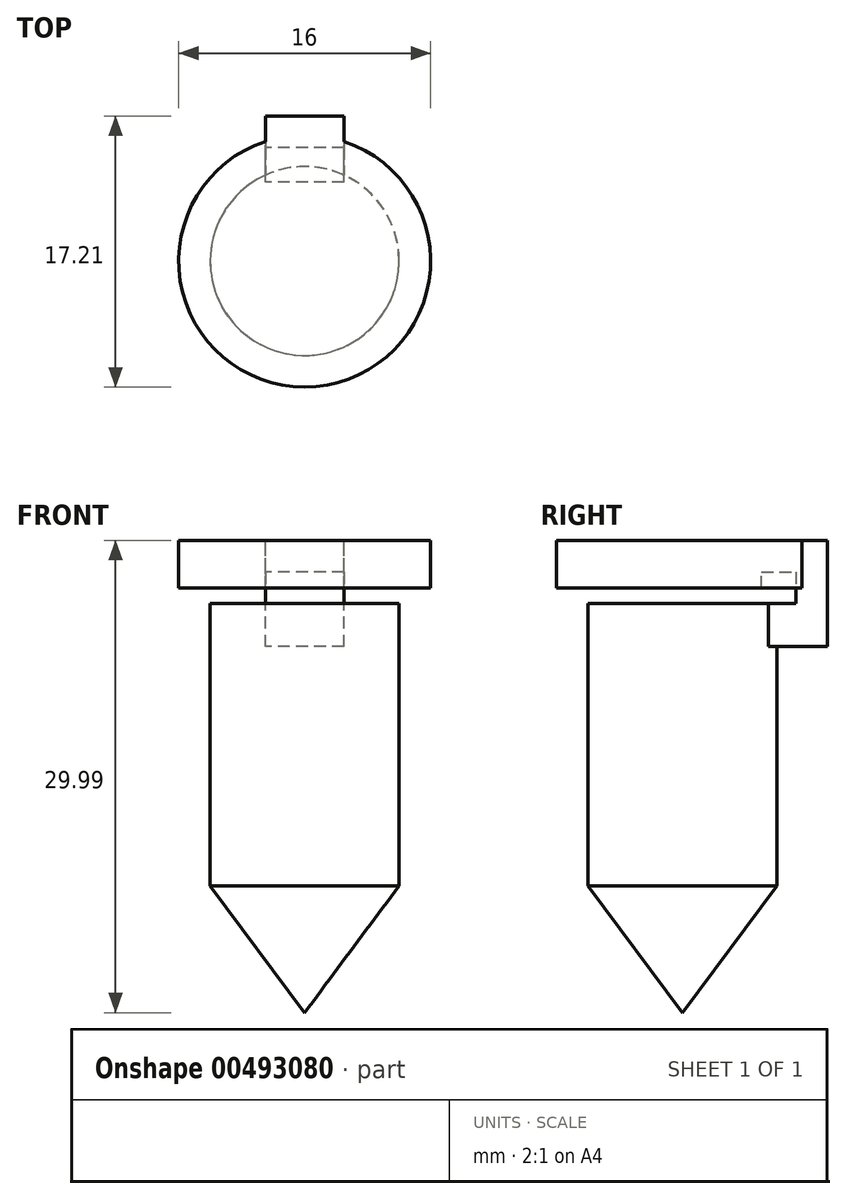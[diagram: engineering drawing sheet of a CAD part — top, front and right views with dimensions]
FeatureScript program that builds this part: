
annotation { "Feature Type Name" : "Feature", "Feature Type Description" : "" }
export const myFeature = defineFeature(function(context is Context, id is Id, definition is map)
    precondition{}
    {
        {
            var Q0;
            Q0=qCreatedBy(makeId("Front.planeOp"),FACE);
            var sketch = newSketch(context, id + "F0", { "sketchPlane" : qUnion([Q0])});
            skLineSegment(sketch, "E0", {"start": v(-6, 14.04) * mm, "end": v(-6, -3.88) * mm});
            skLineSegment(sketch, "E1", {"start": v(-6, -3.88) * mm, "end": v(0, -11.95) * mm});
            skLineSegment(sketch, "E2", {"start": v(-6, 14.04) * mm, "end": v(0, 14.04) * mm});
            skLineSegment(sketch, "E3", {"start": v(0, 14.04) * mm, "end": v(0, -11.95) * mm});
            skSolve(sketch);
        }
        {
            var Q0;
            Q0=makeQuery(id+"F0.imprint","IMPRINT",FACE,{"disambiguationData":[TD([[makeQuery(id+"F0.imprint","IMPRINT",EDGE,{"derivedFrom":sQuery(id+"F0.wireOp",EDGE,"E0")}),1.0]])]});
            var Q1;
            Q1=sQuery(id+"F0.wireOp",EDGE,"E3");
            revolve(context, id + "F1", {"entities" : qUnion([Q0]), "axis" : qUnion([Q1]), "revolveType" : RevolveType.FULL});
        }
        {
            var Q0;
            Q0=qCreatedBy(makeId("Right.planeOp"),FACE);
            var sketch = newSketch(context, id + "F2", { "sketchPlane" : qUnion([Q0])});
            skLineSegment(sketch, "E4", {"start": v(5.2, 11.3) * mm, "end": v(9.2, 11.3) * mm});
            skLineSegment(sketch, "E5", {"start": v(9.2, 11.3) * mm, "end": v(9.2, 18.04) * mm});
            skLineSegment(sketch, "E6", {"start": v(9.2, 18.04) * mm, "end": v(5.01, 18.04) * mm});
            skLineSegment(sketch, "E7", {"start": v(5.01, 18.04) * mm, "end": v(5.01, 16.04) * mm});
            skLineSegment(sketch, "E8", {"start": v(5.01, 16.04) * mm, "end": v(7.2, 16.04) * mm});
            skLineSegment(sketch, "E9", {"start": v(7.2, 16.04) * mm, "end": v(7.2, 14.04) * mm});
            skLineSegment(sketch, "E10", {"start": v(7.2, 14.04) * mm, "end": v(5.01, 14.04) * mm});
            skLineSegment(sketch, "E11", {"start": v(5.01, 14.04) * mm, "end": v(5.2, 11.3) * mm});
            skSolve(sketch);
        }
        {
            var Q0;
            Q0=makeQuery(id+"F2.imprint","IMPRINT",FACE,{"disambiguationData":[TD([[makeQuery(id+"F2.imprint","IMPRINT",EDGE,{"derivedFrom":sQuery(id+"F2.wireOp",EDGE,"E4")}),1.0]])]});
            extrude(context, id + "F3", {"entities" : qUnion([Q0]), "operationType" : NewBodyOperationType.ADD, "endBound" : BoundingType.SYMMETRIC, "depth" : 5 * mm});
        }
        {
            var Q0;
            Q0=makeQuery(id+"F3.opExtrude","SWEPT_FACE",FACE,{"disambiguationData":[OSD([sQuery(id+"F2.wireOp",EDGE,"E6")])]});
            var sketch = newSketch(context, id + "F4", { "sketchPlane" : qUnion([Q0])});
            skCircle(sketch, "E12", {"center": v(0, 0) * mm, "radius": 8 * mm});
            skSolve(sketch);
        }
        {
            var Q0;
            {var subQ1=sQuery(id+"F2.wireOp",EDGE,"E6");var subQ6=makeQuery(id+"F3.opExtrude","SWEPT_EDGE",EDGE,{"disambiguationData":[OSD([subQ1,sQuery(id+"F2.wireOp",EDGE,"E7")])]});Q0=makeQuery(id+"F4.imprint","IMPRINT",FACE,{"disambiguationData":[TD([[makeQuery(id+"F4.imprint","IMPRINT",EDGE,{"derivedFrom":subQ6}),1.0]])]});}
            extrude(context, id + "F5", {"entities" : qUnion([Q0]), "operationType" : NewBodyOperationType.ADD, "oppositeDirection" : true, "depth" : 3 * mm});
        }
    });
